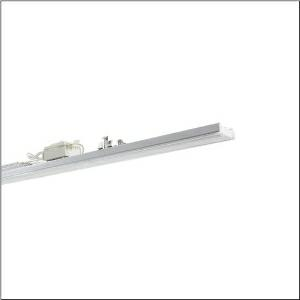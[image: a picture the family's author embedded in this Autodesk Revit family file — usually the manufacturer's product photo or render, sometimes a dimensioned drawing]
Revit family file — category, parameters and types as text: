
# Revit family: licross_r__21_recessed_mo_52tl12cn475g_df1a
name_source: partatom
category: Lighting Fixtures
units: mm (PartAtom-declared; Revit-internal decimal feet)

## family parameters
Cut with Voids When Loaded = No
Host = Face
Light Source = No
Part Type = Normal
Room Calculation Point = No
Round Connector Dimension = Use Diameter
Shared = No

## types (1)
- --- (1 x LED, 7990 lm, 42.6 W, 4000K)
    Apparent Load = 43 VA
    CIE Flux Codes = 72 92 99 100 100
    Color Rendering = 80
    Color Temperature = 4000K
    Default Elevation = 1800 mm
    Description = Licross® 21 Recessed MO, luminaire insert, of sheet steel, galvanised, coil coated, white, length: 1.500mm, width: 66mm, height: 67mm, LED rated luminous flux: 7.990lm, light colour: 840, control gear: ON/OFF Multilumen, CLOi, control gear: ECG Multilumen, with plug, 3-pole, with phase selection, mains connection: 220..240V, AC, 50/60Hz, start of lifetime: 43W, end of service life: 51W, halogen-free wiring, primary optical cover: cover, of PMMA, light emission: direct distribution, primary light characteristic: symmetric, protection rating (complete): IP40, insulation class (complete): insulation class I (protective earthing), certification: CE, ENEC, VDE, UKCA, protection symbol: D if used in an environment without relevant dust loads with corresponding accessories, impact resistance: IK06, permissible ambient temperature for indoor applications: -35..+45°C, corresponds to IFS (International Featured Standards) requirements for safety and quality in the food industry, reducing of maximum allowable ambient temperature of 5°C with ceiling mounting, LABS conformity tested according to VDMA 24364:2018-05, packaging unit: 1 piece
    Height = 58 mm
    Lamp = 1 x LED
    Lamp Light Flux = 7990 lm
    Lamp Power = 42.6 W
    Lamp count = 1
    Length = 1500 mm
    Luminous efficacy = 188 lm/W
    Manufacturer = Siteco
    ModVariant = No
    Model = 52TL12CN475G
    Mounting Place = Ceiling
    Mounting Type = Pendant
    Number of Poles = 1
    OnlyDefault = Yes
    Power Factor = 1
    Product Name = Licross® 21 Recessed MO
    Product group = luminaire insert
    ProductGroupID = 902
    Protection Class = Protection class I
    Protection Degree = IP 40
    RLX_Detail_Level = 1
    RLX_Emergency_Light_Flux = 0 lm
    RLX_Emergency_Type = 0
    RLX_Emergency_Type_DB = No
    RlxData = <blob elided: 22297 chars, md5=d0b68124>
    Socket = socket
    Standby Power = 0 W
    System Light Flux = 7990 lm
    System Power = 43 W
    Type Comments = factory setting: luminous flux: 100 % | (A | C | E) | 99 mA
    Type Image = l_1296930.jpg
    URL = http://relux.com
    VarID = @adj_110594
    Voltage = 0 V
    Weight = 0.00 kg
    Width = 66 mm

## geometry (parser evidence)
native form markers: Blend x4, Sweep x9
no freeform markers — native parametric forms only
